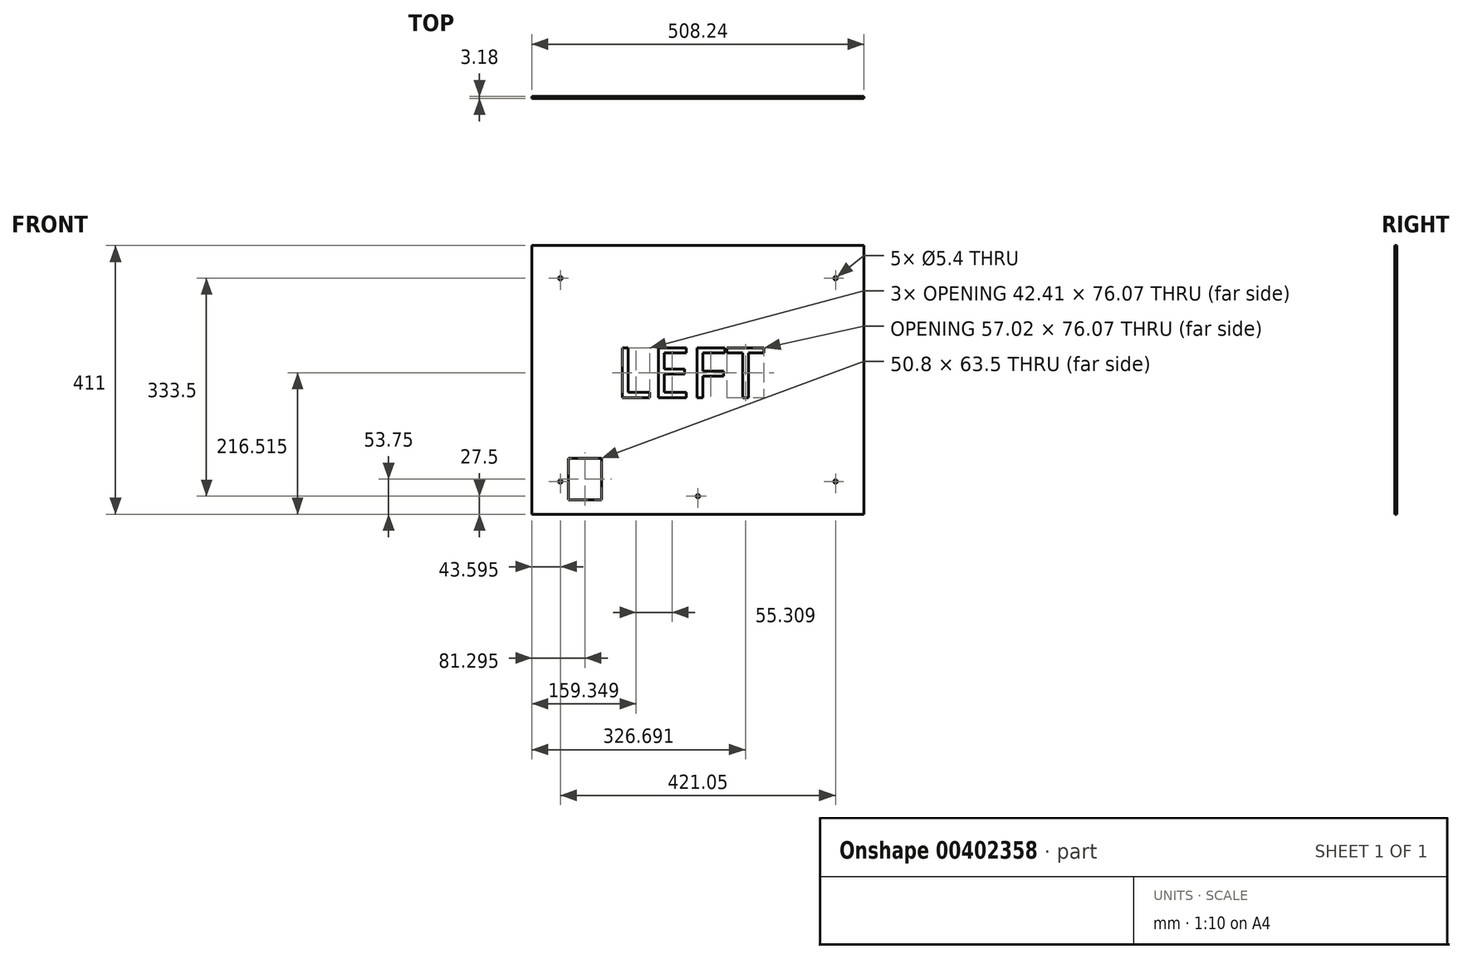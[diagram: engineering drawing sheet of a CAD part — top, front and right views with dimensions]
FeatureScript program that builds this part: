
annotation { "Feature Type Name" : "Feature", "Feature Type Description" : "" }
export const myFeature = defineFeature(function(context is Context, id is Id, definition is map)
    precondition{}
    {
        {
            var Q0;
            Q0=qCreatedBy(makeId("Front.planeOp"),FACE);
            var sketch = newSketch(context, id + "F0", { "sketchPlane" : qUnion([Q0])});
            skLineSegment(sketch, "E0.bottom", {"start": v(-254.12, 205.5) * mm, "end": v(254.12, 205.5) * mm});
            skLineSegment(sketch, "E0.top", {"start": v(-254.13, -205.5) * mm, "end": v(254.12, -205.5) * mm});
            skLineSegment(sketch, "E0.left", {"start": v(-254.12, 205.5) * mm, "end": v(-254.13, -205.5) * mm});
            skLineSegment(sketch, "E0.right", {"start": v(254.12, 205.5) * mm, "end": v(254.12, -205.5) * mm});
            skPoint(sketch, "E0.middle", {"position": v(0, 0) * mm});
            skSolve(sketch);
        }
        {
            var Q0;
            Q0=makeQuery(id+"F0.imprint","IMPRINT",FACE,{"disambiguationData":[TD([[makeQuery(id+"F0.imprint","IMPRINT",EDGE,{"derivedFrom":sQuery(id+"F0.wireOp",EDGE,"E0.bottom")}),-1.0]])]});
            extrude(context, id + "F1", {"entities" : qUnion([Q0]), "depth" : (.125 * 25.4) * mm});
        }
        {
            var Q0;
            Q0=makeQuery(id+"FpBMKNsvPauGnLh_1.boolean.opBoolean","MERGE",FACE,{"derivedFrom":[makeQuery(id+"F1.opExtrude","CAP_FACE",FACE,{"disambiguationData":[OSD([sQuery(id+"F0.wireOp",EDGE,"E0.bottom"),sQuery(id+"F0.wireOp",EDGE,"E0.top"),sQuery(id+"F0.wireOp",EDGE,"E0.left"),sQuery(id+"F0.wireOp",EDGE,"E0.right")])],"isStart":false}),makeQuery(id+"FpBMKNsvPauGnLh_1.opExtrude","CAP_FACE",FACE,{"disambiguationData":[OSD([sQuery(id+"FzWSCRHqbb1aw3Q_1.wireOp",EDGE,"pNUi7Ymo-PIhC-6L1w-etEG-QhCEAS8cRYcq.bottom"),sQuery(id+"FzWSCRHqbb1aw3Q_1.wireOp",EDGE,"pNUi7Ymo-PIhC-6L1w-etEG-QhCEAS8cRYcq.top"),sQuery(id+"FzWSCRHqbb1aw3Q_1.wireOp",EDGE,"pNUi7Ymo-PIhC-6L1w-etEG-QhCEAS8cRYcq.left"),sQuery(id+"FzWSCRHqbb1aw3Q_1.wireOp",EDGE,"pNUi7Ymo-PIhC-6L1w-etEG-QhCEAS8cRYcq.right")])],"isStart":true}),makeQuery(id+"FpBMKNsvPauGnLh_1.opExtrude","CAP_FACE",FACE,{"disambiguationData":[OSD([sQuery(id+"FzWSCRHqbb1aw3Q_1.wireOp",EDGE,"rslhBf2L-x2pj-VNBq-4pd2-VHaR9mQvUz9W.bottom"),sQuery(id+"FzWSCRHqbb1aw3Q_1.wireOp",EDGE,"rslhBf2L-x2pj-VNBq-4pd2-VHaR9mQvUz9W.top"),sQuery(id+"FzWSCRHqbb1aw3Q_1.wireOp",EDGE,"rslhBf2L-x2pj-VNBq-4pd2-VHaR9mQvUz9W.left"),sQuery(id+"FzWSCRHqbb1aw3Q_1.wireOp",EDGE,"rslhBf2L-x2pj-VNBq-4pd2-VHaR9mQvUz9W.right")])],"isStart":true})]});
            var sketch = newSketch(context, id + "F2", { "sketchPlane" : qUnion([Q0])});
            skText(sketch, "E1", { "text": "LEFT", "fontName": "OpenSans-Regular.ttf"});
            const initialGuessF2  = {"E1": [-0.12643, -0.02702, 1, 0, 0.07672]};
            skSetInitialGuess(sketch, initialGuessF2);
            skSolve(sketch);
        }
        {
            var Q0;
            Q0=makeQuery(id+"F2.imprint","IMPRINT",FACE,{"disambiguationData":[TD([[makeQuery(id+"F2.imprint","IMPRINT",EDGE,{"derivedFrom":sQuery(id+"F2.wireOp",EDGE,"E1.sketch_text.stroke-0")}),-1.0]])]});
            var Q1;
            Q1=makeQuery(id+"F2.imprint","IMPRINT",FACE,{"disambiguationData":[TD([[makeQuery(id+"F2.imprint","IMPRINT",EDGE,{"derivedFrom":sQuery(id+"F2.wireOp",EDGE,"E1.sketch_text.stroke-6")}),-1.0]])]});
            var Q2;
            Q2=makeQuery(id+"F2.imprint","IMPRINT",FACE,{"disambiguationData":[TD([[makeQuery(id+"F2.imprint","IMPRINT",EDGE,{"derivedFrom":sQuery(id+"F2.wireOp",EDGE,"E1.sketch_text.stroke-18")}),-1.0]])]});
            var Q3;
            Q3=makeQuery(id+"F2.imprint","IMPRINT",FACE,{"disambiguationData":[TD([[makeQuery(id+"F2.imprint","IMPRINT",EDGE,{"derivedFrom":sQuery(id+"F2.wireOp",EDGE,"E1.sketch_text.stroke-28")}),-1.0]])]});
            extrude(context, id + "F3", {"entities" : qUnion([Q0, Q1, Q2, Q3]), "operationType" : NewBodyOperationType.REMOVE, "oppositeDirection" : true, "depth" : 25 * mm});
        }
        {
            var Q0;
            Q0=makeQuery(id+"FpBMKNsvPauGnLh_1.boolean.opBoolean","MERGE",FACE,{"derivedFrom":[makeQuery(id+"F1.opExtrude","CAP_FACE",FACE,{"disambiguationData":[OSD([sQuery(id+"F0.wireOp",EDGE,"E0.bottom"),sQuery(id+"F0.wireOp",EDGE,"E0.top"),sQuery(id+"F0.wireOp",EDGE,"E0.left"),sQuery(id+"F0.wireOp",EDGE,"E0.right")])],"isStart":false}),makeQuery(id+"FpBMKNsvPauGnLh_1.opExtrude","CAP_FACE",FACE,{"disambiguationData":[OSD([sQuery(id+"FzWSCRHqbb1aw3Q_1.wireOp",EDGE,"pNUi7Ymo-PIhC-6L1w-etEG-QhCEAS8cRYcq.bottom"),sQuery(id+"FzWSCRHqbb1aw3Q_1.wireOp",EDGE,"pNUi7Ymo-PIhC-6L1w-etEG-QhCEAS8cRYcq.top"),sQuery(id+"FzWSCRHqbb1aw3Q_1.wireOp",EDGE,"pNUi7Ymo-PIhC-6L1w-etEG-QhCEAS8cRYcq.left"),sQuery(id+"FzWSCRHqbb1aw3Q_1.wireOp",EDGE,"pNUi7Ymo-PIhC-6L1w-etEG-QhCEAS8cRYcq.right")])],"isStart":true}),makeQuery(id+"FpBMKNsvPauGnLh_1.opExtrude","CAP_FACE",FACE,{"disambiguationData":[OSD([sQuery(id+"FzWSCRHqbb1aw3Q_1.wireOp",EDGE,"rslhBf2L-x2pj-VNBq-4pd2-VHaR9mQvUz9W.bottom"),sQuery(id+"FzWSCRHqbb1aw3Q_1.wireOp",EDGE,"rslhBf2L-x2pj-VNBq-4pd2-VHaR9mQvUz9W.top"),sQuery(id+"FzWSCRHqbb1aw3Q_1.wireOp",EDGE,"rslhBf2L-x2pj-VNBq-4pd2-VHaR9mQvUz9W.left"),sQuery(id+"FzWSCRHqbb1aw3Q_1.wireOp",EDGE,"rslhBf2L-x2pj-VNBq-4pd2-VHaR9mQvUz9W.right")])],"isStart":true})]});
            var sketch = newSketch(context, id + "F4", { "sketchPlane" : qUnion([Q0])});
            skCircle(sketch, "E2", {"center": v(-210.52, 155.5) * mm, "radius": 2.7 * mm});
            skCircle(sketch, "E3", {"center": v(-210.52, -155.5) * mm, "radius": 2.7 * mm});
            skCircle(sketch, "E4", {"center": v(210.53, 155.5) * mm, "radius": 2.7 * mm});
            skCircle(sketch, "E5", {"center": v(210.53, -155.5) * mm, "radius": 2.7 * mm});
            skCircle(sketch, "E6", {"center": v(-0.03, -178) * mm, "radius": 2.7 * mm});
            skLineSegment(sketch, "E7.0.0", {"start": v(-254.13, -205.5) * mm, "end": v(254.12, -205.5) * mm, "construction": true});
            skLineSegment(sketch, "E7.0.2", {"start": v(254.12, -205.5) * mm, "end": v(-254.13, -205.5) * mm, "construction": true});
            skLineSegment(sketch, "E8.0", {"start": v(-254.12, 205.5) * mm, "end": v(-254.13, -205.5) * mm, "construction": true});
            skLineSegment(sketch, "E9.0", {"start": v(254.12, 205.5) * mm, "end": v(254.12, -205.5) * mm, "construction": true});
            skLineSegment(sketch, "E10.0.0", {"start": v(254.12, 205.5) * mm, "end": v(-254.12, 205.5) * mm, "construction": true});
            skLineSegment(sketch, "E10.0.2", {"start": v(-254.12, 205.5) * mm, "end": v(254.12, 205.5) * mm, "construction": true});
            skSolve(sketch);
        }
        {
            var Q0;
            Q0=qSketchRegion(id+"F4",true);
            extrude(context, id + "F5", {"entities" : qUnion([Q0]), "operationType" : NewBodyOperationType.REMOVE, "oppositeDirection" : true, "depth" : 25 * mm});
        }
        {
            var Q0;
            Q0=makeQuery(id+"F1.opExtrude","CAP_FACE",FACE,{"disambiguationData":[OSD([sQuery(id+"F0.wireOp",EDGE,"E0.bottom"),sQuery(id+"F0.wireOp",EDGE,"E0.top"),sQuery(id+"F0.wireOp",EDGE,"E0.left"),sQuery(id+"F0.wireOp",EDGE,"E0.right")])],"isStart":false});
            var sketch = newSketch(context, id + "F6", { "sketchPlane" : qUnion([Q0])});
            skCircle(sketch, "E11", {"center": v(28.85, -176.1) * mm, "radius": 3.38 * mm});
            skSolve(sketch);
        }
        {
            var Q0;
            Q0=makeQuery(id+"F6.imprint","IMPRINT",FACE,{"disambiguationData":[TD([[makeQuery(id+"F6.imprint","IMPRINT",EDGE,{"derivedFrom":sQuery(id+"F6.wireOp",EDGE,"E11")}),-1.0]])]});
            var sketch = newSketch(context, id + "F7", { "sketchPlane" : qUnion([Q0])});
            skLineSegment(sketch, "E12.bottom", {"start": v(-198.23, -120) * mm, "end": v(-147.43, -120) * mm});
            skLineSegment(sketch, "E12.top", {"start": v(-198.23, -183.5) * mm, "end": v(-147.43, -183.5) * mm});
            skLineSegment(sketch, "E12.left", {"start": v(-198.23, -120) * mm, "end": v(-198.23, -183.5) * mm});
            skLineSegment(sketch, "E12.right", {"start": v(-147.43, -120) * mm, "end": v(-147.43, -183.5) * mm});
            skSolve(sketch);
        }
        {
            var Q0;
            Q0=makeQuery(id+"F7.imprint","IMPRINT",FACE,{"disambiguationData":[TD([[makeQuery(id+"F7.imprint","IMPRINT",EDGE,{"derivedFrom":sQuery(id+"F7.wireOp",EDGE,"E12.bottom")}),-1.0]])]});
            extrude(context, id + "F8", {"entities" : qUnion([Q0]), "operationType" : NewBodyOperationType.REMOVE, "oppositeDirection" : true, "depth" : 25 * mm});
        }
    });
